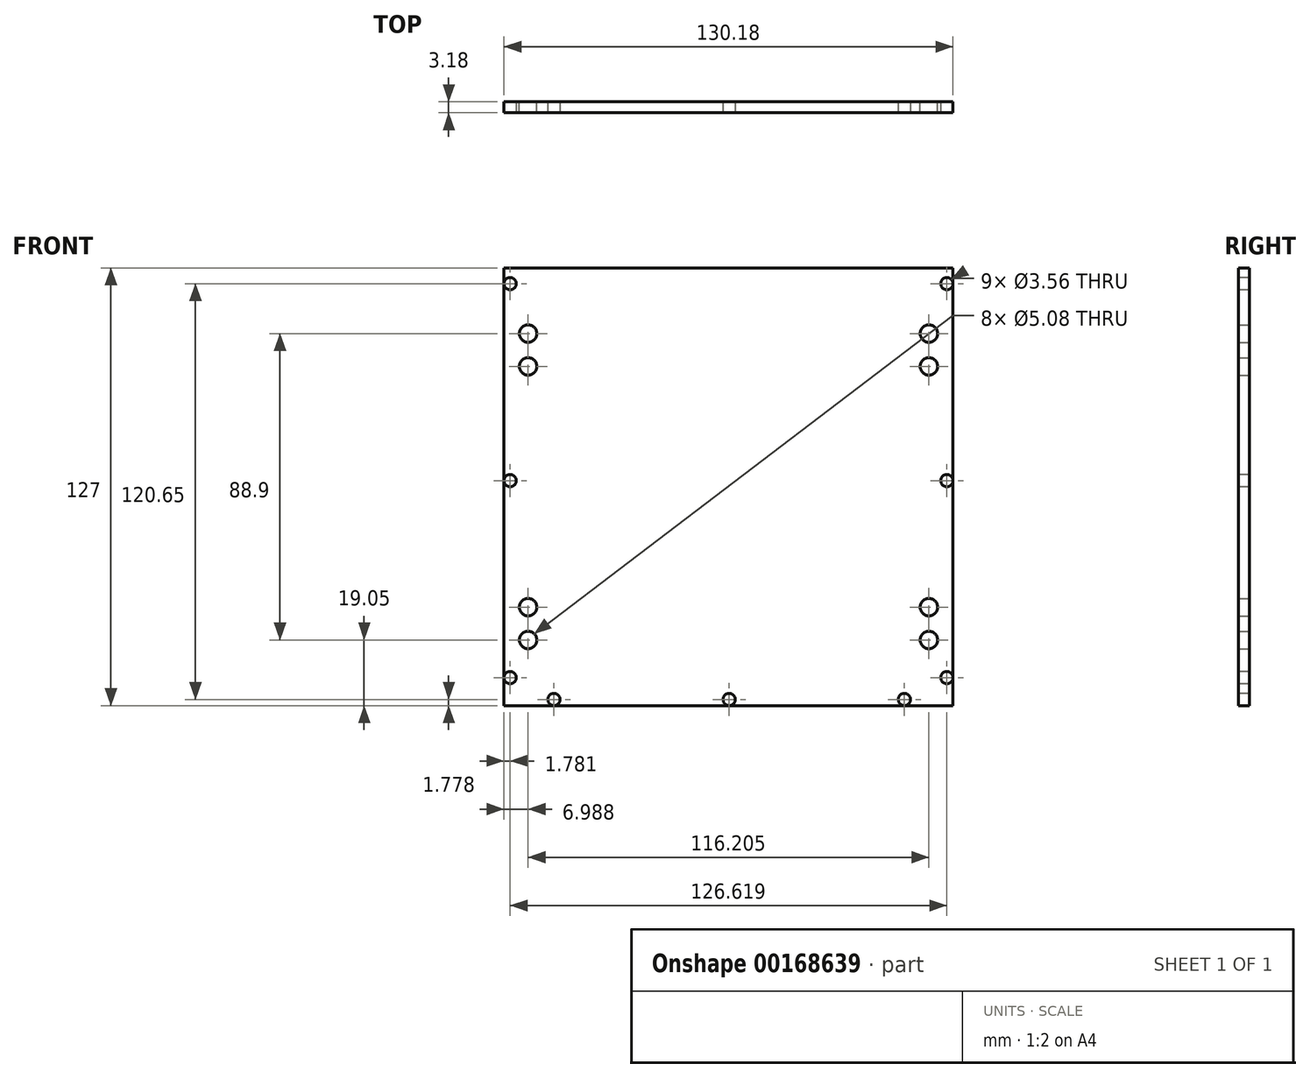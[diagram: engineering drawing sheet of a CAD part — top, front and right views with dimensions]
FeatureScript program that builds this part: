
annotation { "Feature Type Name" : "Feature", "Feature Type Description" : "" }
export const myFeature = defineFeature(function(context is Context, id is Id, definition is map)
    precondition{}
    {
        {
            var Q0;
            Q0=qCreatedBy(makeId("Front.planeOp"),FACE);
            var sketch = newSketch(context, id + "F0", { "sketchPlane" : qUnion([Q0])});
            skLineSegment(sketch, "E0.bottom", {"start": v(65.09, -63.5) * mm, "end": v(-65.09, -63.5) * mm});
            skLineSegment(sketch, "E0.top", {"start": v(65.09, 63.5) * mm, "end": v(-65.09, 63.5) * mm});
            skLineSegment(sketch, "E0.left", {"start": v(65.09, -63.5) * mm, "end": v(65.09, 63.5) * mm});
            skLineSegment(sketch, "E0.right", {"start": v(-65.09, -63.5) * mm, "end": v(-65.09, 63.5) * mm});
            skPoint(sketch, "E0.middle", {"position": v(0, 0) * mm});
            skCircle(sketch, "E1", {"center": v(-58.1, 34.92) * mm, "radius": 2.54 * mm});
            skCircle(sketch, "E2", {"center": v(-58.1, 44.45) * mm, "radius": 2.54 * mm});
            skCircle(sketch, "E3.MirrorC", {"center": v(-58.1, -34.92) * mm, "radius": 2.54 * mm});
            skCircle(sketch, "E4.MirrorC", {"center": v(-58.1, -44.45) * mm, "radius": 2.54 * mm});
            skCircle(sketch, "E5.MirrorC", {"center": v(58.1, 44.45) * mm, "radius": 2.54 * mm});
            skCircle(sketch, "E6.MirrorC", {"center": v(58.1, 34.92) * mm, "radius": 2.54 * mm});
            skCircle(sketch, "E7.MirrorC", {"center": v(58.1, -34.92) * mm, "radius": 2.54 * mm});
            skCircle(sketch, "E8.MirrorC", {"center": v(58.1, -44.45) * mm, "radius": 2.54 * mm});
            skSolve(sketch);
        }
        {
            var Q0;
            {var subQ3=sQuery(id+"F0.wireOp",EDGE,"E0.top");Q0=makeQuery(id+"F0.imprint","IMPRINT",FACE,{"disambiguationData":[TD([[makeQuery(id+"F0.imprint","IMPRINT",EDGE,{"derivedFrom":subQ3}),1.0]])]});}
            extrude(context, id + "F1", {"entities" : qUnion([Q0]), "endBound" : BoundingType.SYMMETRIC, "depth" : 3.17 * mm});
        }
        {
            var Q0;
            Q0=makeQuery(id+"F1.opExtrude","CAP_FACE",FACE,{"disambiguationData":[OSD([sQuery(id+"F0.wireOp",EDGE,"E0.bottom"),sQuery(id+"F0.wireOp",EDGE,"E0.top"),sQuery(id+"F0.wireOp",EDGE,"E0.left"),sQuery(id+"F0.wireOp",EDGE,"E0.right"),sQuery(id+"F0.wireOp",EDGE,"E1"),sQuery(id+"F0.wireOp",EDGE,"E2"),sQuery(id+"F0.wireOp",EDGE,"E3.MirrorC"),sQuery(id+"F0.wireOp",EDGE,"E4.MirrorC"),sQuery(id+"F0.wireOp",EDGE,"E5.MirrorC"),sQuery(id+"F0.wireOp",EDGE,"E6.MirrorC"),sQuery(id+"F0.wireOp",EDGE,"E7.MirrorC"),sQuery(id+"F0.wireOp",EDGE,"E8.MirrorC")])],"isStart":false});
            var sketch = newSketch(context, id + "F2", { "sketchPlane" : qUnion([Q0])});
            skCircle(sketch, "E9", {"center": v(-63.3, -55.37) * mm, "radius": 1.78 * mm});
            skCircle(sketch, "E10.0.1.0", {"center": v(-63.3, 1.78) * mm, "radius": 1.78 * mm});
            skCircle(sketch, "E10.0.2.0", {"center": v(-63.3, 58.93) * mm, "radius": 1.78 * mm});
            skLineSegment(sketch, "E10.direction1", {"start": v(-63.3, -55.37) * mm, "end": v(-36.32, -55.37) * mm, "construction": true});
            skLineSegment(sketch, "E10.direction2", {"start": v(-63.3, -55.37) * mm, "end": v(-63.3, 1.78) * mm, "construction": true});
            skCircle(sketch, "E11.MirrorC", {"center": v(63.3, -55.37) * mm, "radius": 1.78 * mm});
            skCircle(sketch, "E12.MirrorC", {"center": v(63.3, 1.78) * mm, "radius": 1.78 * mm});
            skCircle(sketch, "E13.MirrorC", {"center": v(63.3, 58.93) * mm, "radius": 1.78 * mm});
            skCircle(sketch, "E14", {"center": v(-50.6, -61.72) * mm, "radius": 1.78 * mm});
            skCircle(sketch, "E15.1.0.0", {"center": v(0.2, -61.72) * mm, "radius": 1.78 * mm});
            skCircle(sketch, "E15.2.0.0", {"center": v(51, -61.72) * mm, "radius": 1.78 * mm});
            skLineSegment(sketch, "E15.direction1", {"start": v(-50.6, -61.72) * mm, "end": v(0.2, -61.72) * mm, "construction": true});
            skSolve(sketch);
        }
        {
            var Q0;
            Q0=sQuery(id+"F2.wireOp",VERTEX,"E10.0.2.0.center");
            var Q1;
            Q1=sQuery(id+"F2.wireOp",VERTEX,"E10.direction2.end");
            var Q2;
            Q2=sQuery(id+"F2.wireOp",VERTEX,"E9.center");
            var Q3;
            Q3=sQuery(id+"F2.wireOp",VERTEX,"E15.direction1.start");
            var Q4;
            Q4=sQuery(id+"F2.wireOp",VERTEX,"E15.direction1.end");
            var Q5;
            Q5=sQuery(id+"F2.wireOp",VERTEX,"E15.2.0.0.center");
            var Q6;
            Q6=sQuery(id+"F2.wireOp",VERTEX,"E11.MirrorC.center");
            var Q7;
            Q7=sQuery(id+"F2.wireOp",VERTEX,"E12.MirrorC.center");
            var Q8;
            Q8=sQuery(id+"F2.wireOp",VERTEX,"E13.MirrorC.center");
            var Q9;
            Q9=makeQuery(id+"F1.opExtrude","SWEPT_BODY",BODY,{"disambiguationData":[OSD([sQuery(id+"F0.wireOp",EDGE,"E0.bottom"),sQuery(id+"F0.wireOp",EDGE,"E0.top"),sQuery(id+"F0.wireOp",EDGE,"E0.left"),sQuery(id+"F0.wireOp",EDGE,"E0.right"),sQuery(id+"F0.wireOp",EDGE,"E1"),sQuery(id+"F0.wireOp",EDGE,"E2"),sQuery(id+"F0.wireOp",EDGE,"E3.MirrorC"),sQuery(id+"F0.wireOp",EDGE,"E4.MirrorC"),sQuery(id+"F0.wireOp",EDGE,"E5.MirrorC"),sQuery(id+"F0.wireOp",EDGE,"E6.MirrorC"),sQuery(id+"F0.wireOp",EDGE,"E7.MirrorC"),sQuery(id+"F0.wireOp",EDGE,"E8.MirrorC")])]});
            hole(context, id + "F3", {"style" : HoleStyle.SIMPLE, "endStyle" : HoleEndStyle.THROUGH, "holeDiameter" : 3.56 * mm, "locations" : qUnion([Q0, Q1, Q2, Q3, Q4, Q5, Q6, Q7, Q8]), "scope" : qUnion([Q9]), "isTappedThrough" : true});
        }
    });
